# Revit family: Moni table
name_source: partatom
category: Furniture
revit_build: Autodesk Revit 2015 (Build: 20140606_1530(x64)
units: mm (PartAtom-declared; Revit-internal decimal feet)

## types (8) — shared parameters
Frame material = RAL 9006 Abloy Aluminum grey
GA annotation visibility = No
GA visibility = Yes
Manufacturer = Isku Oy
Studs material = Rubber
Table top height = 727 mm  [stored 2.38517 ft]
Table top thickness = 26 mm
Table top visibility = Yes
Type Comments = Available as antimicrobial
URL = www.isku.fi

## per-type parameters (varying)
| type | C-Table top | Depth | Five legs visibility | O6 annotation visibility | O9 annotation visibility | Square annotation visibility | Square table visibility | Table top type | Two legs visibility | Width |
| Moni A16 | No | 800 mm  [stored 2.62467 ft] | No | No | No | Yes | Yes | Table covers : A16 | Yes | 1600 mm  [stored 5.24934 ft] |
| Moni A18 | No | 800 mm  [stored 2.62467 ft] | No | No | No | Yes | Yes | Table covers : A18 | Yes | 1800 mm  [stored 5.90551 ft] |
| Moni C14 | Yes | 700 mm  [stored 2.29659 ft] | No | No | No | Yes | No | Table covers : C14 | Yes | 1400 mm  [stored 4.59318 ft] |
| Moni C16 | Yes | 700 mm  [stored 2.29659 ft] | No | No | No | Yes | No | Table covers : C16 | Yes | 1600 mm  [stored 5.24934 ft] |
| Moni C18 | Yes | 700 mm  [stored 2.29659 ft] | No | No | No | Yes | No | Table covers : C18 | Yes | 1800 mm  [stored 5.90551 ft] |
| Moni O6 | No | 700 mm  [stored 2.29659 ft] | Yes | Yes | No | No | No | Table covers : O6 | No | 1800 mm  [stored 5.90551 ft] |
| Moni O9 | No | 700 mm  [stored 2.29659 ft] | Yes | No | Yes | No | No | Table covers : O9 | No | 1800 mm  [stored 5.90551 ft] |
| Moni C12 | Yes | 700 mm  [stored 2.29659 ft] | No | No | No | Yes | No | Table covers : C12 | Yes | 1200 mm  [stored 3.93701 ft] |

note: [stored X ft] marks values corroborated as IEEE doubles in the binary element streams (Revit-internal decimal feet)

## geometry (parser evidence)
native form markers: Sweep x13
no freeform markers — native parametric forms only
